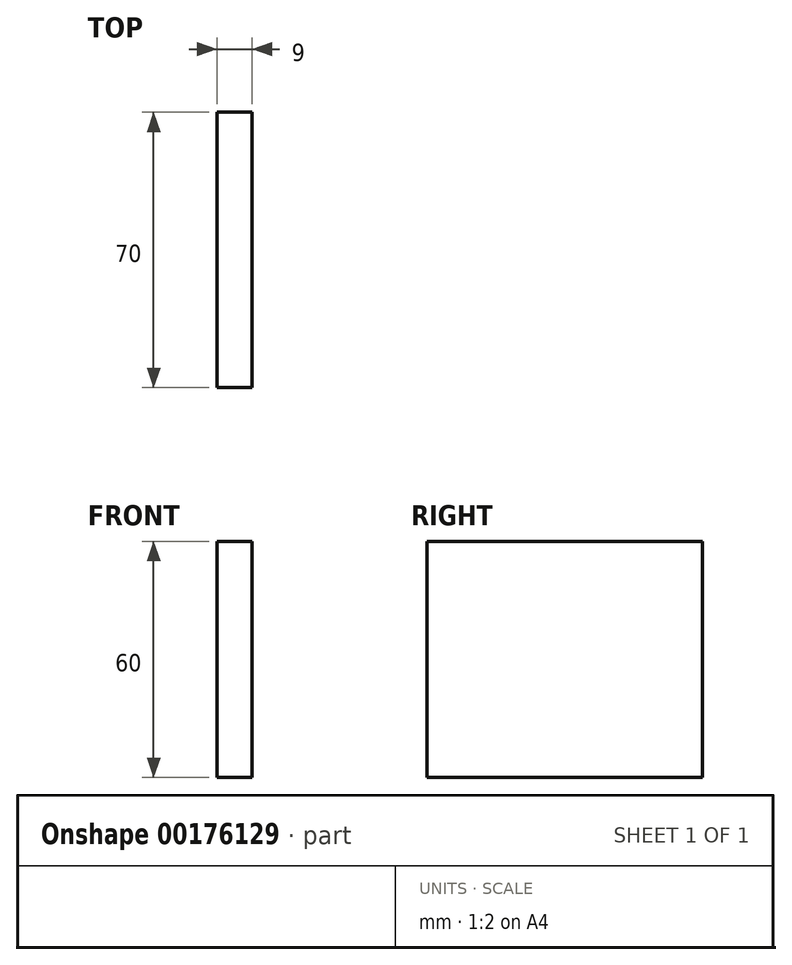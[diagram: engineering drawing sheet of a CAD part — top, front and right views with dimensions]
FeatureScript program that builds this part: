
annotation { "Feature Type Name" : "Feature", "Feature Type Description" : "" }
export const myFeature = defineFeature(function(context is Context, id is Id, definition is map)
    precondition{}
    {
        {
            var Q0;
            Q0=qCreatedBy(makeId("Right.planeOp"),FACE);
            var sketch = newSketch(context, id + "F0", { "sketchPlane" : qUnion([Q0])});
            skLineSegment(sketch, "E0.bottom", {"start": v(0, 0) * mm, "end": v(80, 0) * mm});
            skLineSegment(sketch, "E0.top", {"start": v(0, 60) * mm, "end": v(80, 60) * mm});
            skLineSegment(sketch, "E0.left", {"start": v(0, 0) * mm, "end": v(0, 60) * mm});
            skLineSegment(sketch, "E0.right", {"start": v(80, 0) * mm, "end": v(80, 60) * mm});
            skSolve(sketch);
        }
        {
            var Q0;
            Q0 = qSketchRegion(id + "F0", true);
            extrude(context, id + "F1", {"entities" : qUnion([Q0]), "depth" : 9 * mm});
        }
        {
            var Q0;
            Q0=makeQuery(id+"F1.opExtrude","CAP_FACE",FACE,{"disambiguationData":[OSD([sQuery(id+"F0.wireOp",EDGE,"E0.bottom"),sQuery(id+"F0.wireOp",EDGE,"E0.top"),sQuery(id+"F0.wireOp",EDGE,"E0.left"),sQuery(id+"F0.wireOp",EDGE,"E0.right")])],"isStart":false});
            var sketch = newSketch(context, id + "F2", { "sketchPlane" : qUnion([Q0])});
            skLineSegment(sketch, "E1", {"start": v(40, 0) * mm, "end": v(40, 60) * mm});
            skLineSegment(sketch, "E2", {"start": v(40, 60) * mm, "end": v(5, 60) * mm});
            skLineSegment(sketch, "E3", {"start": v(40, 60) * mm, "end": v(75, 60) * mm});
            skLineSegment(sketch, "E4", {"start": v(40, 30) * mm, "end": v(23.34, 30) * mm});
            skPoint(sketch, "E4.endSnap0", {"position": v(40, 30) * mm});
            skLineSegment(sketch, "E5.bottom", {"start": v(5, 60) * mm, "end": v(75, 60) * mm});
            skLineSegment(sketch, "E5.top", {"start": v(5, 51) * mm, "end": v(75, 51) * mm});
            skLineSegment(sketch, "E5.left", {"start": v(5, 60) * mm, "end": v(5, 51) * mm});
            skLineSegment(sketch, "E5.right", {"start": v(75, 60) * mm, "end": v(75, 51) * mm});
            skLineSegment(sketch, "E6.MirrorCS", {"start": v(5, 42) * mm, "end": v(5, 51) * mm});
            skLineSegment(sketch, "E7.MirrorCS", {"start": v(5, 9) * mm, "end": v(75, 9) * mm});
            skLineSegment(sketch, "E8.MirrorCS", {"start": v(5, 0) * mm, "end": v(5, 9) * mm});
            skLineSegment(sketch, "E9.MirrorCS", {"start": v(75, 0) * mm, "end": v(75, 9) * mm});
            skLineSegment(sketch, "E10.MirrorCS", {"start": v(5, 0) * mm, "end": v(75, 0) * mm});
            skLineSegment(sketch, "E11", {"start": v(75, 51) * mm, "end": v(80, 51) * mm});
            skLineSegment(sketch, "E12", {"start": v(5, 51) * mm, "end": v(0, 51) * mm});
            skLineSegment(sketch, "E13", {"start": v(5, 9) * mm, "end": v(0, 9) * mm});
            skLineSegment(sketch, "E14", {"start": v(75, 9) * mm, "end": v(80, 9) * mm});
            skSolve(sketch);
        }
        {
            var Q0;
            {var subQ0=sQuery(id+"F2.wireOp",EDGE,"E5.right");Q0=makeQuery(id+"F2.imprint","IMPRINT",FACE,{"disambiguationData":[TD([[makeQuery(id+"F2.imprint","IMPRINT",EDGE,{"derivedFrom":subQ0}),1.0]])]});}
            var Q1;
            {var subQ0=sQuery(id+"F2.wireOp",EDGE,"E5.left");Q1=makeQuery(id+"F2.imprint","IMPRINT",FACE,{"disambiguationData":[TD([[makeQuery(id+"F2.imprint","IMPRINT",EDGE,{"derivedFrom":subQ0}),-1.0]])]});}
            var Q2;
            {var subQ0=sQuery(id+"F2.wireOp",EDGE,"E8.MirrorCS");Q2=makeQuery(id+"F2.imprint","IMPRINT",FACE,{"disambiguationData":[TD([[makeQuery(id+"F2.imprint","IMPRINT",EDGE,{"derivedFrom":subQ0}),1.0]])]});}
            var Q3;
            {var subQ0=sQuery(id+"F2.wireOp",EDGE,"E9.MirrorCS");Q3=makeQuery(id+"F2.imprint","IMPRINT",FACE,{"disambiguationData":[TD([[makeQuery(id+"F2.imprint","IMPRINT",EDGE,{"derivedFrom":subQ0}),-1.0]])]});}
            extrude(context, id + "F3", {"entities" : qUnion([Q0, Q1, Q2, Q3]), "operationType" : NewBodyOperationType.ADD, "depth" : 5 * mm});
        }
        {
            var Q0;
            {var subQ0=sQuery(id+"F0.wireOp",EDGE,"E0.right");var subQ1=makeQuery(id+"F1.opExtrude","CAP_EDGE",EDGE,{"disambiguationData":[OSD([subQ0])],"isStart":false});Q0=makeQuery(id+"F3.boolean.opBoolean","MERGE",FACE,{"derivedFrom":[makeQuery(id+"F1.opExtrude","SWEPT_FACE",FACE,{"disambiguationData":[OSD([subQ0])]}),makeQuery(id+"F3.opExtrude","SWEPT_FACE",FACE,{"disambiguationData":[OSD([subQ0]),TDD([makeQuery(id+"F2.imprint","IMPRINT",EDGE,{"disambiguationData":[TD([[makeQuery(id+"F2.imprint","INTERSECT",VERTEX,{"derivedFrom":[makeQuery(id+"F1.opExtrude","CAP_EDGE",EDGE,{"disambiguationData":[OSD([sQuery(id+"F0.wireOp",EDGE,"E0.bottom")])],"isStart":false}),subQ1]}),-1.0]])],"derivedFrom":subQ1})])]}),makeQuery(id+"F3.opExtrude","SWEPT_FACE",FACE,{"disambiguationData":[OSD([subQ0]),TDD([makeQuery(id+"F2.imprint","IMPRINT",EDGE,{"disambiguationData":[TD([[makeQuery(id+"F2.imprint","INTERSECT",VERTEX,{"derivedFrom":[makeQuery(id+"F1.opExtrude","CAP_EDGE",EDGE,{"disambiguationData":[OSD([sQuery(id+"F0.wireOp",EDGE,"E0.top")])],"isStart":false}),subQ1]}),1.0]])],"derivedFrom":subQ1})])]})]});}
            var sketch = newSketch(context, id + "F4", { "sketchPlane" : qUnion([Q0])});
            skLineSegment(sketch, "E15.bottom", {"start": v(-14, 60) * mm, "end": v(0, 60) * mm});
            skLineSegment(sketch, "E15.top", {"start": v(-14, 0) * mm, "end": v(0, 0) * mm});
            skLineSegment(sketch, "E15.left", {"start": v(-14, 60) * mm, "end": v(-14, 0) * mm});
            skLineSegment(sketch, "E15.right", {"start": v(0, 60) * mm, "end": v(0, 0) * mm});
            skSolve(sketch);
        }
        {
            var Q0;
            {var subQ2=sQuery(id+"F4.wireOp",EDGE,"E15.bottom");Q0=makeQuery(id+"F4.imprint","IMPRINT",FACE,{"disambiguationData":[TD([[makeQuery(id+"F4.imprint","IMPRINT",EDGE,{"derivedFrom":subQ2}),-1.0]])]});}
            var Q1;
            Q1=makeQuery(id+"F3.opExtrude","SWEPT_FACE",FACE,{"disambiguationData":[OSD([sQuery(id+"F2.wireOp",EDGE,"E5.right")])]});
            extrude(context, id + "F5", {"entities" : qUnion([Q0]), "operationType" : NewBodyOperationType.REMOVE, "endBound" : BoundingType.UP_TO_SURFACE, "oppositeDirection" : true, "endBoundEntityFace" : qUnion([Q1]), "depth" : 25 * mm});
        }
        {
            var Q0;
            {var subQ0=sQuery(id+"F0.wireOp",EDGE,"E0.left");var subQ1=makeQuery(id+"F1.opExtrude","CAP_EDGE",EDGE,{"disambiguationData":[OSD([subQ0])],"isStart":false});Q0=makeQuery(id+"F3.boolean.opBoolean","MERGE",FACE,{"derivedFrom":[makeQuery(id+"F1.opExtrude","SWEPT_FACE",FACE,{"disambiguationData":[OSD([subQ0])]}),makeQuery(id+"F3.opExtrude","SWEPT_FACE",FACE,{"disambiguationData":[OSD([subQ0]),TDD([makeQuery(id+"F2.imprint","IMPRINT",EDGE,{"disambiguationData":[TD([[makeQuery(id+"F2.imprint","INTERSECT",VERTEX,{"derivedFrom":[makeQuery(id+"F1.opExtrude","CAP_EDGE",EDGE,{"disambiguationData":[OSD([sQuery(id+"F0.wireOp",EDGE,"E0.bottom")])],"isStart":false}),subQ1]}),-1.0]])],"derivedFrom":subQ1})])]}),makeQuery(id+"F3.opExtrude","SWEPT_FACE",FACE,{"disambiguationData":[OSD([subQ0]),TDD([makeQuery(id+"F2.imprint","IMPRINT",EDGE,{"disambiguationData":[TD([[makeQuery(id+"F2.imprint","INTERSECT",VERTEX,{"derivedFrom":[makeQuery(id+"F1.opExtrude","CAP_EDGE",EDGE,{"disambiguationData":[OSD([sQuery(id+"F0.wireOp",EDGE,"E0.top")])],"isStart":false}),subQ1]}),1.0]])],"derivedFrom":subQ1})])]})]});}
            var Q1;
            Q1=makeQuery(id+"F3.opExtrude","SWEPT_FACE",FACE,{"disambiguationData":[OSD([sQuery(id+"F2.wireOp",EDGE,"E5.left")])]});
            extrude(context, id + "F6", {"entities" : qUnion([Q0]), "operationType" : NewBodyOperationType.REMOVE, "endBound" : BoundingType.UP_TO_SURFACE, "oppositeDirection" : true, "endBoundEntityFace" : qUnion([Q1]), "depth" : 25 * mm});
        }
    });
